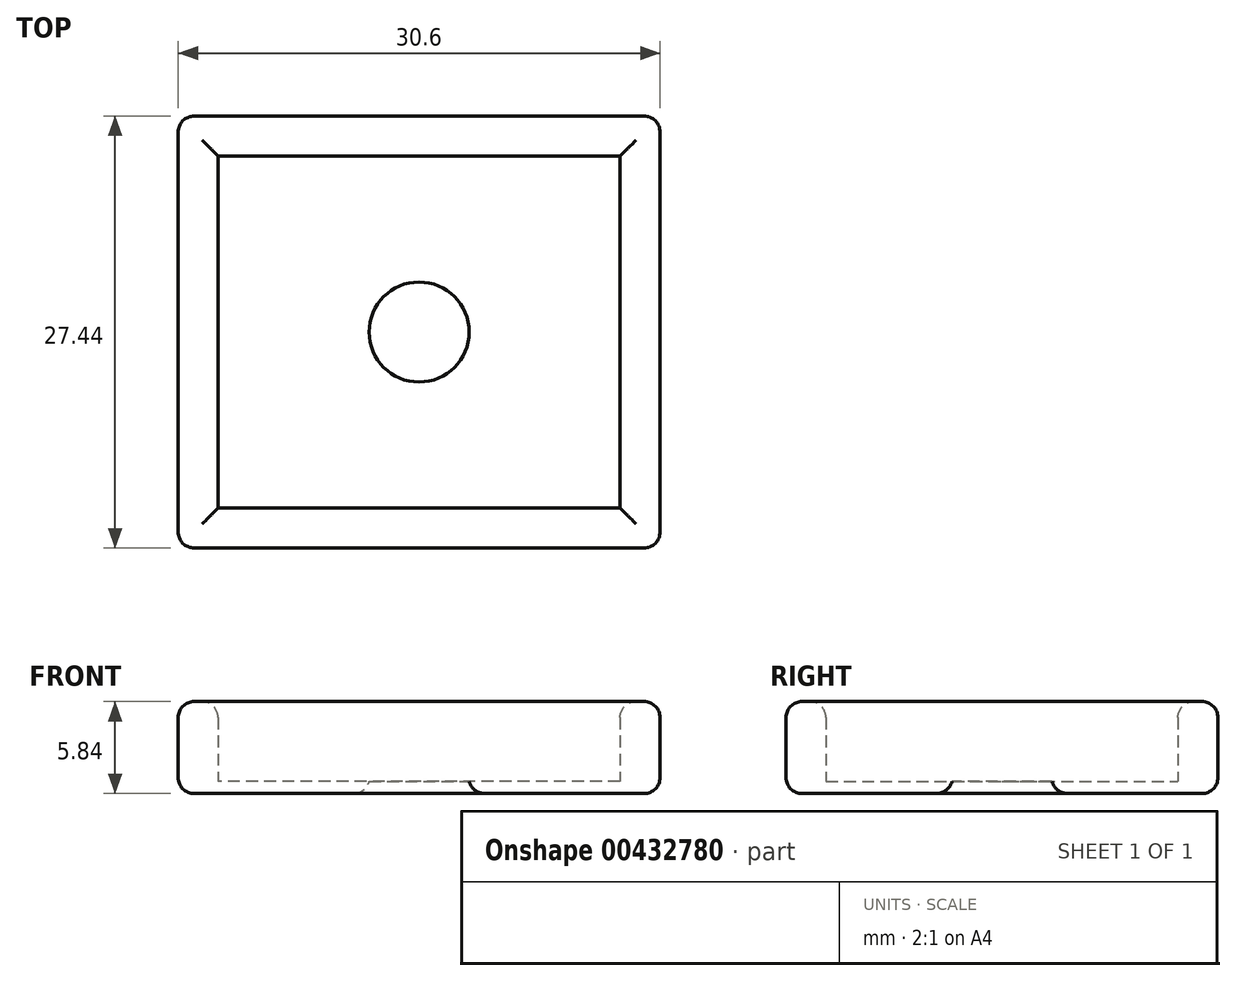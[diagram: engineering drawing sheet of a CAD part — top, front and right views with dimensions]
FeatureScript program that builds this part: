
annotation { "Feature Type Name" : "Feature", "Feature Type Description" : "" }
export const myFeature = defineFeature(function(context is Context, id is Id, definition is map)
    precondition{}
    {
        {
            var Q0;
            Q0=qCreatedBy(makeId("Top.planeOp"),FACE);
            var sketch = newSketch(context, id + "F0", { "sketchPlane" : qUnion([Q0])});
            skLineSegment(sketch, "E0.bottom", {"start": v(12.76, -11.18) * mm, "end": v(-12.76, -11.18) * mm});
            skLineSegment(sketch, "E0.top", {"start": v(12.76, 11.18) * mm, "end": v(-12.76, 11.18) * mm});
            skLineSegment(sketch, "E0.left", {"start": v(12.76, -11.18) * mm, "end": v(12.76, 11.18) * mm});
            skLineSegment(sketch, "E0.right", {"start": v(-12.76, -11.18) * mm, "end": v(-12.76, 11.18) * mm});
            skPoint(sketch, "E0.middle", {"position": v(0, 0) * mm});
            skLineSegment(sketch, "E1.bottom", {"start": v(15.3, -13.72) * mm, "end": v(-15.3, -13.72) * mm});
            skLineSegment(sketch, "E1.top", {"start": v(15.3, 13.72) * mm, "end": v(-15.3, 13.72) * mm});
            skLineSegment(sketch, "E1.left", {"start": v(15.3, -13.72) * mm, "end": v(15.3, 13.72) * mm});
            skLineSegment(sketch, "E1.right", {"start": v(-15.3, -13.72) * mm, "end": v(-15.3, 13.72) * mm});
            skSolve(sketch);
        }
        {
            var Q0;
            Q0 = qSketchRegion(id + "F0", true);
            extrude(context, id + "F1", {"entities" : qUnion([Q0]), "depth" : 5.08 * mm});
        }
        {
            var Q0;
            Q0=makeQuery(id+"F1.opExtrude","CAP_FACE",FACE,{"disambiguationData":[OSD([sQuery(id+"F0.wireOp",EDGE,"E0.bottom"),sQuery(id+"F0.wireOp",EDGE,"E0.top"),sQuery(id+"F0.wireOp",EDGE,"E0.left"),sQuery(id+"F0.wireOp",EDGE,"E0.right"),sQuery(id+"F0.wireOp",EDGE,"E1.bottom"),sQuery(id+"F0.wireOp",EDGE,"E1.top"),sQuery(id+"F0.wireOp",EDGE,"E1.left"),sQuery(id+"F0.wireOp",EDGE,"E1.right")])],"isStart":true});
            var sketch = newSketch(context, id + "F2", { "sketchPlane" : qUnion([Q0])});
            skLineSegment(sketch, "E2.bottom", {"start": v(-15.3, 13.72) * mm, "end": v(15.3, 13.72) * mm});
            skLineSegment(sketch, "E2.top", {"start": v(-15.3, -13.72) * mm, "end": v(15.3, -13.72) * mm});
            skLineSegment(sketch, "E2.left", {"start": v(-15.3, 13.72) * mm, "end": v(-15.3, -13.72) * mm});
            skLineSegment(sketch, "E2.right", {"start": v(15.3, 13.72) * mm, "end": v(15.3, -13.72) * mm});
            skCircle(sketch, "E3", {"center": v(0, 0) * mm, "radius": 3.18 * mm});
            skSolve(sketch);
        }
        {
            var Q0;
            Q0 = qSketchRegion(id + "F2", true);
            extrude(context, id + "F3", {"entities" : qUnion([Q0]), "operationType" : NewBodyOperationType.ADD, "depth" : 0.76 * mm});
        }
        {
            var Q0;
            Q0=makeQuery(id+"F3.boolean.opBoolean","MERGE",FACE,{"derivedFrom":[makeQuery(id+"F1.opExtrude","SWEPT_FACE",FACE,{"disambiguationData":[OSD([sQuery(id+"F0.wireOp",EDGE,"E1.bottom")])]}),makeQuery(id+"F3.opExtrude","SWEPT_FACE",FACE,{"disambiguationData":[OSD([sQuery(id+"F2.wireOp",EDGE,"E2.bottom")])]})]});
            var Q1;
            Q1=makeQuery(id+"F3.opExtrude","CAP_FACE",FACE,{"disambiguationData":[OSD([sQuery(id+"F2.wireOp",EDGE,"E2.bottom"),sQuery(id+"F2.wireOp",EDGE,"E2.top"),sQuery(id+"F2.wireOp",EDGE,"E2.left"),sQuery(id+"F2.wireOp",EDGE,"E2.right"),sQuery(id+"F2.wireOp",EDGE,"E3")])],"isStart":false});
            var Q2;
            Q2=makeQuery(id+"F3.boolean.opBoolean","MERGE",FACE,{"derivedFrom":[makeQuery(id+"F1.opExtrude","SWEPT_FACE",FACE,{"disambiguationData":[OSD([sQuery(id+"F0.wireOp",EDGE,"E1.top")])]}),makeQuery(id+"F3.opExtrude","SWEPT_FACE",FACE,{"disambiguationData":[OSD([sQuery(id+"F2.wireOp",EDGE,"E2.top")])]})]});
            var Q3;
            Q3=makeQuery(id+"F3.boolean.opBoolean","MERGE",FACE,{"derivedFrom":[makeQuery(id+"F1.opExtrude","SWEPT_FACE",FACE,{"disambiguationData":[OSD([sQuery(id+"F0.wireOp",EDGE,"E1.right")])]}),makeQuery(id+"F3.opExtrude","SWEPT_FACE",FACE,{"disambiguationData":[OSD([sQuery(id+"F2.wireOp",EDGE,"E2.left")])]})]});
            var Q4;
            Q4=makeQuery(id+"F3.boolean.opBoolean","MERGE",FACE,{"derivedFrom":[makeQuery(id+"F1.opExtrude","SWEPT_FACE",FACE,{"disambiguationData":[OSD([sQuery(id+"F0.wireOp",EDGE,"E1.left")])]}),makeQuery(id+"F3.opExtrude","SWEPT_FACE",FACE,{"disambiguationData":[OSD([sQuery(id+"F2.wireOp",EDGE,"E2.right")])]})]});
            var Q5;
            Q5=makeQuery(id+"F1.opExtrude","CAP_EDGE",EDGE,{"disambiguationData":[OSD([sQuery(id+"F0.wireOp",EDGE,"E0.right")])],"isStart":false});
            var Q6;
            Q6=makeQuery(id+"F1.opExtrude","CAP_EDGE",EDGE,{"disambiguationData":[OSD([sQuery(id+"F0.wireOp",EDGE,"E0.top")])],"isStart":false});
            var Q7;
            Q7=makeQuery(id+"F1.opExtrude","CAP_EDGE",EDGE,{"disambiguationData":[OSD([sQuery(id+"F0.wireOp",EDGE,"E0.bottom")])],"isStart":false});
            var Q8;
            Q8=makeQuery(id+"F1.opExtrude","CAP_EDGE",EDGE,{"disambiguationData":[OSD([sQuery(id+"F0.wireOp",EDGE,"E0.left")])],"isStart":false});
            fillet(context, id + "F4", {"entities" : qUnion([Q0, Q1, Q2, Q3, Q4, Q5, Q6, Q7, Q8]), "radius" : 1.02 * mm, "tangentPropagation" : true, "allowEdgeOverflow" : false});
        }
    });
